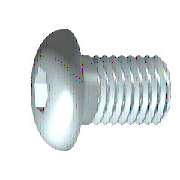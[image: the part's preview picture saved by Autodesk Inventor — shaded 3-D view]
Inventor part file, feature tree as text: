
AUTODESK INVENTOR PART (.ipt)
format: ipt  version: 2013 (Build 170138000, 138)  size: 198,656 bytes
history: native  units: mm (DEFAULTED — no unit token found)
features: sketch x2, extrude x1, plane x1, fillet x1
ambient origin geometry x7: Origin, YZ Plane, XY Plane, X Axis, Y Axis, Z Axis, Center Point
bodies: Solid1 (feature_tree), Body (feature_tree)
feature tree (5):
  extrude  "Slot"  Depth=1.59014mm
  plane  "Work Plane1"
  fillet  "Fillet2"  Radius=2.2098mm
  sketch  "Sketch1"  dims[d1=7.93476mm d2=1.59014mm d3=2.2098mm]
  sketch  "Sketch2"  dims[d4=1.3208mm d5=60.0deg d6=4.1656mm d7=4.1656mm d8=2.756963mm d9=7.9248mm d10=90.0deg d11=10.0mm d12=0.0mm d13=7.93476mm d14=0.0mm d15=0.486918mm d16=0.486918mm d17=1.9558mm d19=0.0mm d26=9.525mm d27=45.0deg d28=0.0mm d29=0.0mm d30=0.1mm]
